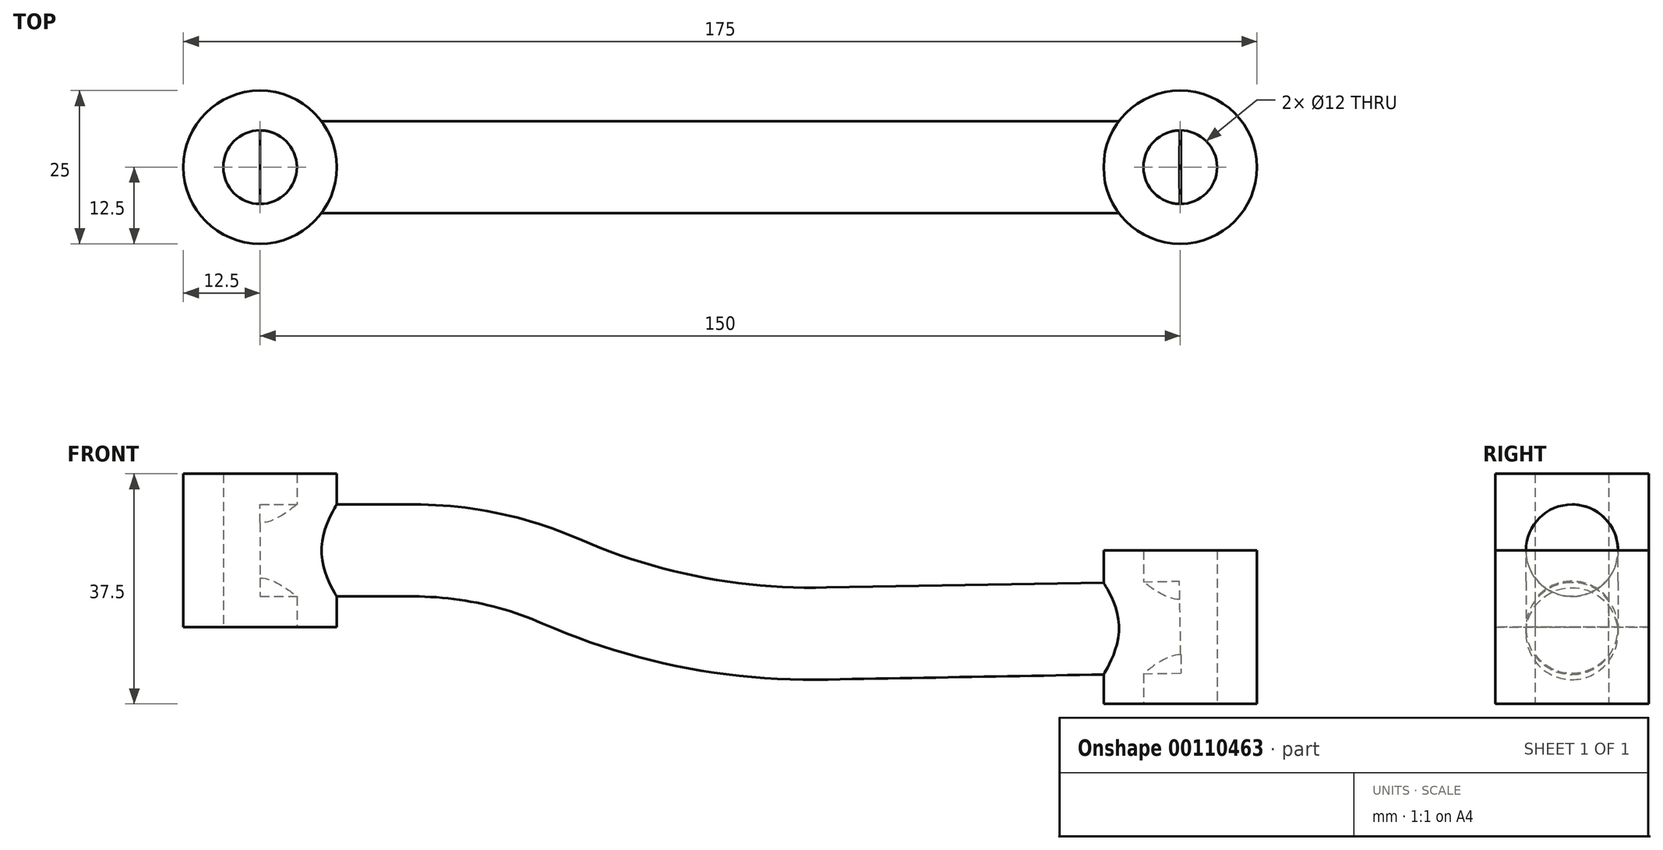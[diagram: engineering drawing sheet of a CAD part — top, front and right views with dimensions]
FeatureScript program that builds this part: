
annotation { "Feature Type Name" : "Feature", "Feature Type Description" : "" }
export const myFeature = defineFeature(function(context is Context, id is Id, definition is map)
    precondition{}
    {
        {
            var Q0;
            Q0=qCreatedBy(makeId("Top.planeOp"),FACE);
            var sketch = newSketch(context, id + "F0", { "sketchPlane" : qUnion([Q0])});
            skCircle(sketch, "E0", {"center": v(0, 0) * mm, "radius": 6 * mm});
            skCircle(sketch, "E1", {"center": v(0, 0) * mm, "radius": 12.5 * mm});
            skCircle(sketch, "E2", {"center": v(150, 0) * mm, "radius": 6 * mm});
            skCircle(sketch, "E3", {"center": v(150, 0) * mm, "radius": 12.5 * mm});
            skSolve(sketch);
        }
        {
            var Q0;
            Q0=makeQuery(id+"F0.imprint","IMPRINT",FACE,{"disambiguationData":[TD([[makeQuery(id+"F0.imprint","IMPRINT",EDGE,{"derivedFrom":sQuery(id+"F0.wireOp",EDGE,"E0")}),-1.0]])]});
            extrude(context, id + "F1", {"entities" : qUnion([Q0]), "depth" : 25 * mm});
        }
        {
            var Q0;
            Q0=makeQuery(id+"F0.imprint","IMPRINT",FACE,{"disambiguationData":[TD([[makeQuery(id+"F0.imprint","IMPRINT",EDGE,{"derivedFrom":sQuery(id+"F0.wireOp",EDGE,"E2")}),-1.0]])]});
            extrude(context, id + "F2", {"entities" : qUnion([Q0]), "endBound" : BoundingType.SYMMETRIC, "depth" : 25 * mm});
        }
        {
            var Q0;
            Q0=qCreatedBy(makeId("Front.planeOp"),FACE);
            var sketch = newSketch(context, id + "F3", { "sketchPlane" : qUnion([Q0])});
            skLineSegment(sketch, "E4", {"start": v(0, 12.5) * mm, "end": v(25, 12.5) * mm});
            skLineSegment(sketch, "E5", {"start": v(150, 0) * mm, "end": v(92.45, -1.04) * mm});
            skArc(sketch, "E6", {"start": v(25, 12.5) * mm, "mid": v(37.28, 11.23) * mm, "end": v(49.04, 7.47) * mm});
            skArc(sketch, "E7", {"start": v(49.04, 7.47) * mm, "mid": v(70.28, 0.84) * mm, "end": v(92.45, -1.04) * mm});
            skSolve(sketch);
        }
        {
            var Q0;
            Q0=qCreatedBy(makeId("Right.planeOp"),FACE);
            var sketch = newSketch(context, id + "F4", { "sketchPlane" : qUnion([Q0])});
            skCircle(sketch, "E8", {"center": v(0, 12.5) * mm, "radius": 7.5 * mm});
            skSolve(sketch);
        }
        {
            var Q0;
            Q0 = qSketchRegion(id + "F4", true);
            var Q1;
            Q1 = qConstructionFilter(qBodyType(qCreatedBy(id + "F3" ,EDGE), BodyType.WIRE), ConstructionObject.NO);
            sweep(context, id + "F5", {"operationType" : NewBodyOperationType.ADD, "profiles" : qUnion([Q0]), "path" : qUnion([Q1])});
        }
    });
